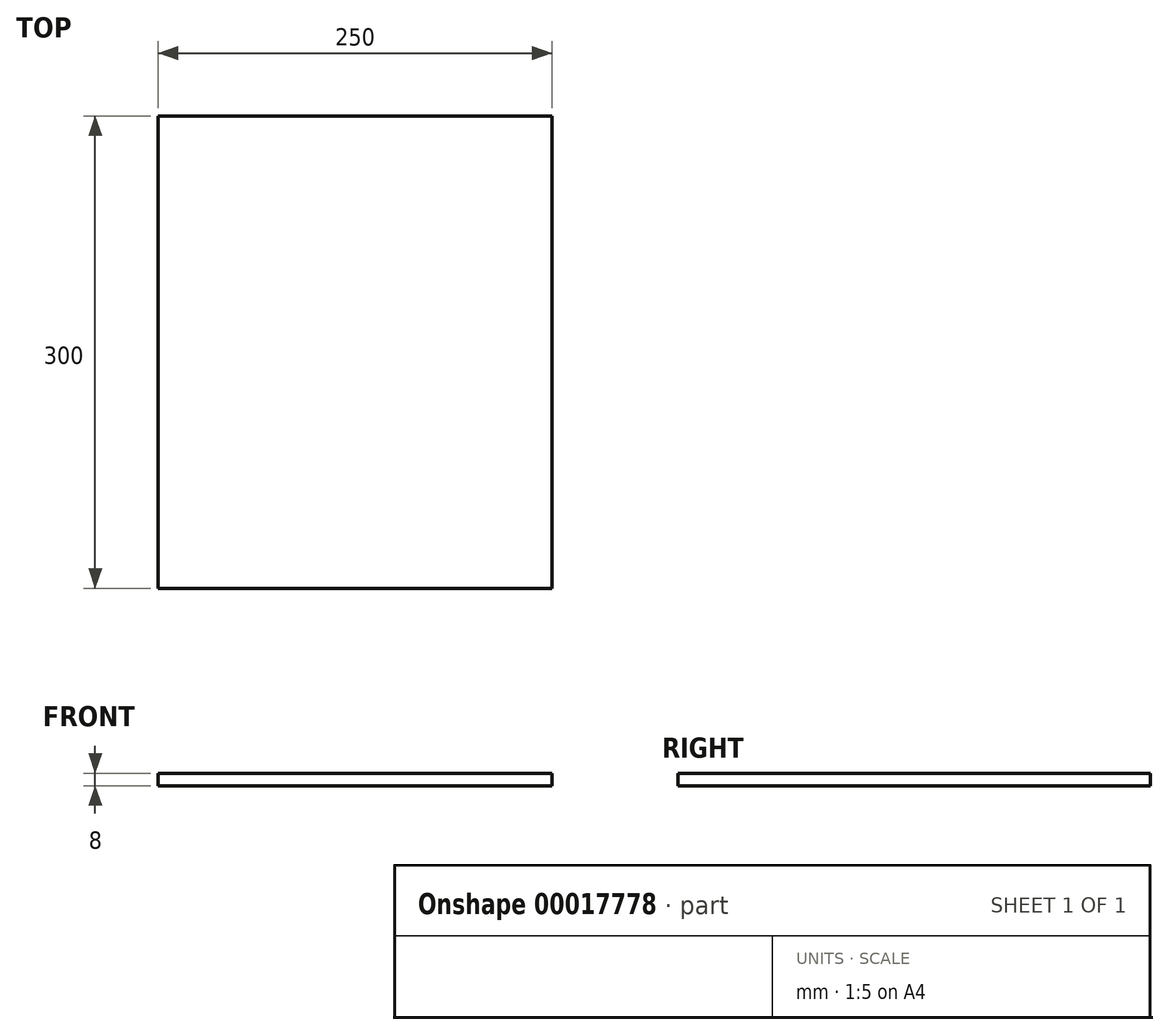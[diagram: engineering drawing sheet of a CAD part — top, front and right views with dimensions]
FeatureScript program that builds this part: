
annotation { "Feature Type Name" : "Feature", "Feature Type Description" : "" }
export const myFeature = defineFeature(function(context is Context, id is Id, definition is map)
    precondition{}
    {
        {
            var Q0;
            Q0=qCreatedBy(makeId("Top.planeOp"),FACE);
            var sketch = newSketch(context, id + "F0", { "sketchPlane" : qUnion([Q0])});
            skLineSegment(sketch, "E0.bottom", {"start": v(0, 0) * mm, "end": v(250, 0) * mm});
            skLineSegment(sketch, "E0.top", {"start": v(0, 300) * mm, "end": v(250, 300) * mm});
            skLineSegment(sketch, "E0.left", {"start": v(0, 0) * mm, "end": v(0, 300) * mm});
            skLineSegment(sketch, "E0.right", {"start": v(250, 0) * mm, "end": v(250, 300) * mm});
            skSolve(sketch);
        }
        {
            var Q0;
            Q0=qSketchRegion(id+"F0",true);
            extrude(context, id + "F1", {"entities" : qUnion([Q0]), "depth" : 8 * mm});
        }
    });
